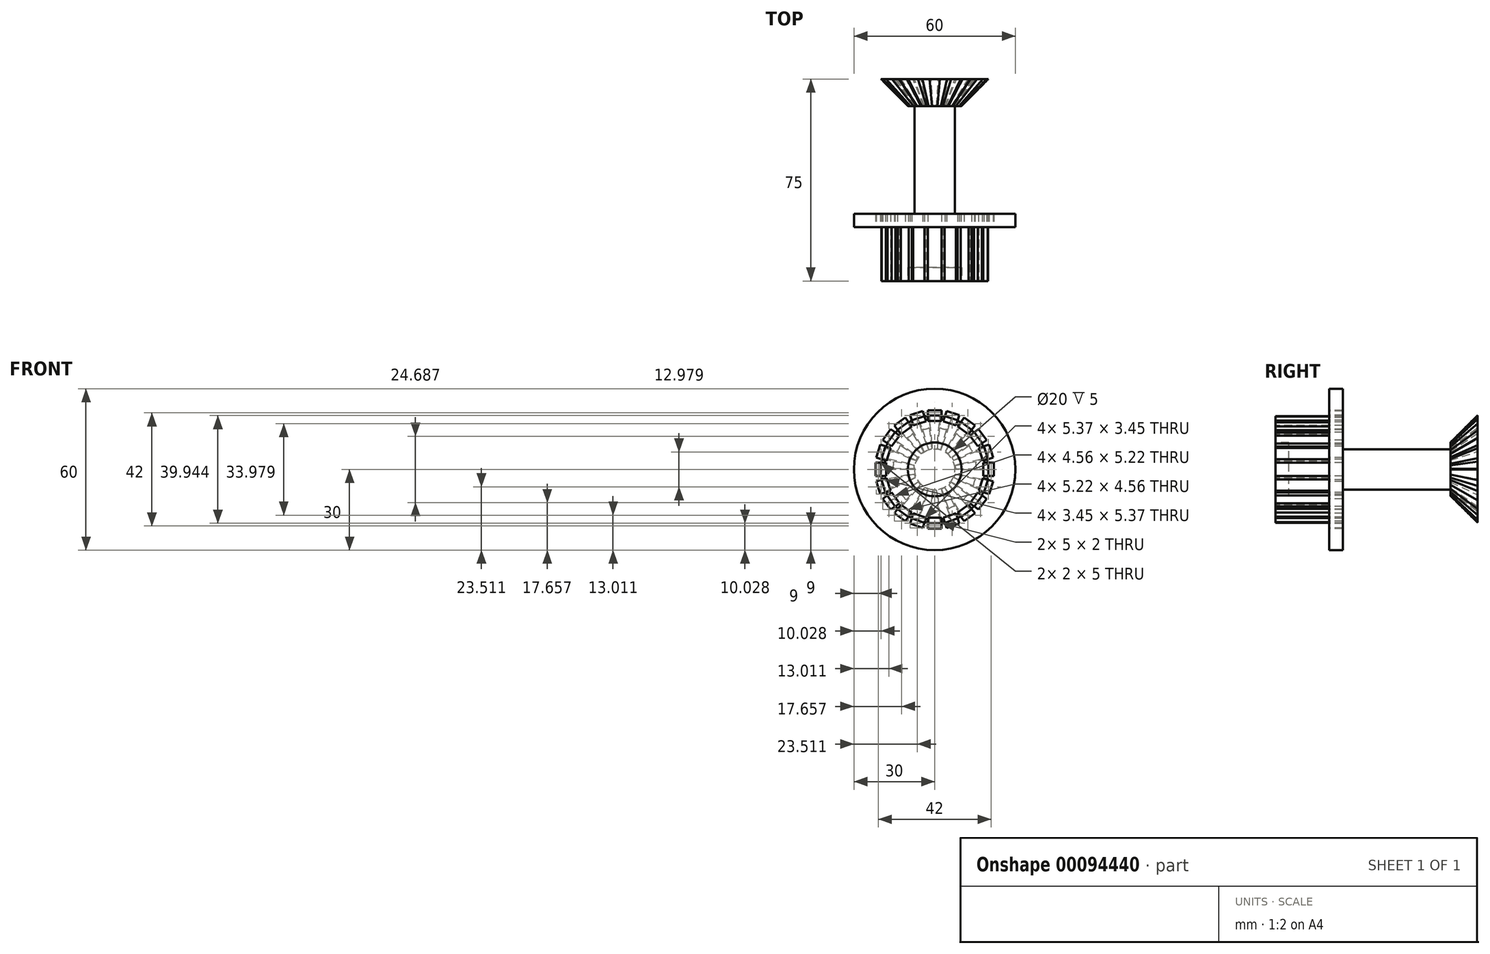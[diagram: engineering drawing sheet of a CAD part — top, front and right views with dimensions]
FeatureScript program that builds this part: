
annotation { "Feature Type Name" : "Feature", "Feature Type Description" : "" }
export const myFeature = defineFeature(function(context is Context, id is Id, definition is map)
    precondition{}
    {
        {
            var Q0;
            Q0=qCreatedBy(makeId("Front.planeOp"),FACE);
            var sketch = newSketch(context, id + "F0", { "sketchPlane" : qUnion([Q0])});
            skCircle(sketch, "E0", {"center": v(0, 0) * mm, "radius": 20 * mm});
            skSolve(sketch);
        }
        {
            var Q0;
            Q0=makeQuery(id+"F0.imprint","IMPRINT",FACE,{"disambiguationData":[TD([[makeQuery(id+"F0.imprint","IMPRINT",EDGE,{"derivedFrom":sQuery(id+"F0.wireOp",EDGE,"E0")}),1.0]])]});
            extrude(context, id + "F1", {"entities" : qUnion([Q0]), "depth" : 20 * mm});
        }
        {
            var Q0;
            Q0=makeQuery(id+"F1.opExtrude","CAP_FACE",FACE,{"disambiguationData":[OSD([sQuery(id+"F0.wireOp",EDGE,"E0")])],"isStart":true});
            var sketch = newSketch(context, id + "F2", { "sketchPlane" : qUnion([Q0])});
            skCircle(sketch, "E1", {"center": v(0, 0) * mm, "radius": 30 * mm});
            skSolve(sketch);
        }
        {
            var Q0;
            Q0 = qSketchRegion(id + "F2", true);
            extrude(context, id + "F3", {"entities" : qUnion([Q0]), "operationType" : NewBodyOperationType.ADD, "depth" : 5 * mm});
        }
        {
            var Q0;
            Q0=makeQuery(id+"F3.opExtrude","CAP_FACE",FACE,{"disambiguationData":[OSD([sQuery(id+"F2.wireOp",EDGE,"E1")])],"isStart":true});
            var sketch = newSketch(context, id + "F4", { "sketchPlane" : qUnion([Q0])});
            skLineSegment(sketch, "E2", {"start": v(-2.5, 21) * mm, "end": v(-2.5, 22) * mm});
            skLineSegment(sketch, "E3", {"start": v(-2.5, 22) * mm, "end": v(2.5, 22) * mm});
            skLineSegment(sketch, "E4", {"start": v(2.5, 22) * mm, "end": v(2.5, 20) * mm});
            skLineSegment(sketch, "E5", {"start": v(2.5, 20) * mm, "end": v(-2.5, 20) * mm});
            skLineSegment(sketch, "E6", {"start": v(-2.5, 20) * mm, "end": v(-2.5, 21) * mm});
            skLineSegment(sketch, "E7.1.0", {"start": v(-9.18, 20.15) * mm, "end": v(-4.42, 21.7) * mm});
            skLineSegment(sketch, "E7.1.1", {"start": v(-3.8, 19.8) * mm, "end": v(-8.56, 18.25) * mm});
            skLineSegment(sketch, "E7.1.2", {"start": v(-8.56, 18.25) * mm, "end": v(-8.87, 19.2) * mm});
            skLineSegment(sketch, "E7.1.3", {"start": v(-8.87, 19.2) * mm, "end": v(-9.18, 20.15) * mm});
            skLineSegment(sketch, "E7.1.4", {"start": v(-4.42, 21.7) * mm, "end": v(-3.8, 19.8) * mm});
            skLineSegment(sketch, "E7.2.0", {"start": v(-14.95, 16.33) * mm, "end": v(-10.9, 19.27) * mm});
            skLineSegment(sketch, "E7.2.1", {"start": v(-9.73, 17.65) * mm, "end": v(-13.78, 14.71) * mm});
            skLineSegment(sketch, "E7.2.2", {"start": v(-13.78, 14.71) * mm, "end": v(-14.37, 15.52) * mm});
            skLineSegment(sketch, "E7.2.3", {"start": v(-14.37, 15.52) * mm, "end": v(-14.95, 16.33) * mm});
            skLineSegment(sketch, "E7.2.4", {"start": v(-10.9, 19.27) * mm, "end": v(-9.73, 17.65) * mm});
            skLineSegment(sketch, "E7.3.0", {"start": v(-19.27, 10.9) * mm, "end": v(-16.33, 14.95) * mm});
            skLineSegment(sketch, "E7.3.1", {"start": v(-14.71, 13.78) * mm, "end": v(-17.65, 9.73) * mm});
            skLineSegment(sketch, "E7.3.2", {"start": v(-17.65, 9.73) * mm, "end": v(-18.46, 10.32) * mm});
            skLineSegment(sketch, "E7.3.3", {"start": v(-18.46, 10.32) * mm, "end": v(-19.27, 10.9) * mm});
            skLineSegment(sketch, "E7.3.4", {"start": v(-16.33, 14.95) * mm, "end": v(-14.71, 13.78) * mm});
            skLineSegment(sketch, "E7.4.0", {"start": v(-21.7, 4.42) * mm, "end": v(-20.15, 9.18) * mm});
            skLineSegment(sketch, "E7.4.1", {"start": v(-18.25, 8.56) * mm, "end": v(-19.8, 3.8) * mm});
            skLineSegment(sketch, "E7.4.2", {"start": v(-19.8, 3.8) * mm, "end": v(-20.74, 4.11) * mm});
            skLineSegment(sketch, "E7.4.3", {"start": v(-20.74, 4.11) * mm, "end": v(-21.7, 4.42) * mm});
            skLineSegment(sketch, "E7.4.4", {"start": v(-20.15, 9.18) * mm, "end": v(-18.25, 8.56) * mm});
            skLineSegment(sketch, "E7.5.0", {"start": v(-22, -2.5) * mm, "end": v(-22, 2.5) * mm});
            skLineSegment(sketch, "E7.5.1", {"start": v(-20, 2.5) * mm, "end": v(-20, -2.5) * mm});
            skLineSegment(sketch, "E7.5.2", {"start": v(-20, -2.5) * mm, "end": v(-21, -2.5) * mm});
            skLineSegment(sketch, "E7.5.3", {"start": v(-21, -2.5) * mm, "end": v(-22, -2.5) * mm});
            skLineSegment(sketch, "E7.5.4", {"start": v(-22, 2.5) * mm, "end": v(-20, 2.5) * mm});
            skLineSegment(sketch, "E7.6.0", {"start": v(-20.15, -9.18) * mm, "end": v(-21.7, -4.42) * mm});
            skLineSegment(sketch, "E7.6.1", {"start": v(-19.8, -3.8) * mm, "end": v(-18.25, -8.56) * mm});
            skLineSegment(sketch, "E7.6.2", {"start": v(-18.25, -8.56) * mm, "end": v(-19.2, -8.87) * mm});
            skLineSegment(sketch, "E7.6.3", {"start": v(-19.2, -8.87) * mm, "end": v(-20.15, -9.18) * mm});
            skLineSegment(sketch, "E7.6.4", {"start": v(-21.7, -4.42) * mm, "end": v(-19.8, -3.8) * mm});
            skLineSegment(sketch, "E7.7.0", {"start": v(-16.33, -14.95) * mm, "end": v(-19.27, -10.9) * mm});
            skLineSegment(sketch, "E7.7.1", {"start": v(-17.65, -9.73) * mm, "end": v(-14.71, -13.78) * mm});
            skLineSegment(sketch, "E7.7.2", {"start": v(-14.71, -13.78) * mm, "end": v(-15.52, -14.37) * mm});
            skLineSegment(sketch, "E7.7.3", {"start": v(-15.52, -14.37) * mm, "end": v(-16.33, -14.95) * mm});
            skLineSegment(sketch, "E7.7.4", {"start": v(-19.27, -10.9) * mm, "end": v(-17.65, -9.73) * mm});
            skLineSegment(sketch, "E7.8.0", {"start": v(-10.9, -19.27) * mm, "end": v(-14.95, -16.33) * mm});
            skLineSegment(sketch, "E7.8.1", {"start": v(-13.78, -14.71) * mm, "end": v(-9.73, -17.65) * mm});
            skLineSegment(sketch, "E7.8.2", {"start": v(-9.73, -17.65) * mm, "end": v(-10.32, -18.46) * mm});
            skLineSegment(sketch, "E7.8.3", {"start": v(-10.32, -18.46) * mm, "end": v(-10.9, -19.27) * mm});
            skLineSegment(sketch, "E7.8.4", {"start": v(-14.95, -16.33) * mm, "end": v(-13.78, -14.71) * mm});
            skLineSegment(sketch, "E7.9.0", {"start": v(-4.42, -21.7) * mm, "end": v(-9.18, -20.15) * mm});
            skLineSegment(sketch, "E7.9.1", {"start": v(-8.56, -18.25) * mm, "end": v(-3.8, -19.8) * mm});
            skLineSegment(sketch, "E7.9.2", {"start": v(-3.8, -19.8) * mm, "end": v(-4.11, -20.74) * mm});
            skLineSegment(sketch, "E7.9.3", {"start": v(-4.11, -20.74) * mm, "end": v(-4.42, -21.7) * mm});
            skLineSegment(sketch, "E7.9.4", {"start": v(-9.18, -20.15) * mm, "end": v(-8.56, -18.25) * mm});
            skLineSegment(sketch, "E7.10.0", {"start": v(2.5, -22) * mm, "end": v(-2.5, -22) * mm});
            skLineSegment(sketch, "E7.10.1", {"start": v(-2.5, -20) * mm, "end": v(2.5, -20) * mm});
            skLineSegment(sketch, "E7.10.2", {"start": v(2.5, -20) * mm, "end": v(2.5, -21) * mm});
            skLineSegment(sketch, "E7.10.3", {"start": v(2.5, -21) * mm, "end": v(2.5, -22) * mm});
            skLineSegment(sketch, "E7.10.4", {"start": v(-2.5, -22) * mm, "end": v(-2.5, -20) * mm});
            skLineSegment(sketch, "E7.11.0", {"start": v(9.18, -20.15) * mm, "end": v(4.42, -21.7) * mm});
            skLineSegment(sketch, "E7.11.1", {"start": v(3.8, -19.8) * mm, "end": v(8.56, -18.25) * mm});
            skLineSegment(sketch, "E7.11.2", {"start": v(8.56, -18.25) * mm, "end": v(8.87, -19.2) * mm});
            skLineSegment(sketch, "E7.11.3", {"start": v(8.87, -19.2) * mm, "end": v(9.18, -20.15) * mm});
            skLineSegment(sketch, "E7.11.4", {"start": v(4.42, -21.7) * mm, "end": v(3.8, -19.8) * mm});
            skLineSegment(sketch, "E7.12.0", {"start": v(14.95, -16.33) * mm, "end": v(10.9, -19.27) * mm});
            skLineSegment(sketch, "E7.12.1", {"start": v(9.73, -17.65) * mm, "end": v(13.78, -14.71) * mm});
            skLineSegment(sketch, "E7.12.2", {"start": v(13.78, -14.71) * mm, "end": v(14.37, -15.52) * mm});
            skLineSegment(sketch, "E7.12.3", {"start": v(14.37, -15.52) * mm, "end": v(14.95, -16.33) * mm});
            skLineSegment(sketch, "E7.12.4", {"start": v(10.9, -19.27) * mm, "end": v(9.73, -17.65) * mm});
            skLineSegment(sketch, "E7.13.0", {"start": v(19.27, -10.9) * mm, "end": v(16.33, -14.95) * mm});
            skLineSegment(sketch, "E7.13.1", {"start": v(14.71, -13.78) * mm, "end": v(17.65, -9.73) * mm});
            skLineSegment(sketch, "E7.13.2", {"start": v(17.65, -9.73) * mm, "end": v(18.46, -10.32) * mm});
            skLineSegment(sketch, "E7.13.3", {"start": v(18.46, -10.32) * mm, "end": v(19.27, -10.9) * mm});
            skLineSegment(sketch, "E7.13.4", {"start": v(16.33, -14.95) * mm, "end": v(14.71, -13.78) * mm});
            skLineSegment(sketch, "E7.14.0", {"start": v(21.7, -4.42) * mm, "end": v(20.15, -9.18) * mm});
            skLineSegment(sketch, "E7.14.1", {"start": v(18.25, -8.56) * mm, "end": v(19.8, -3.8) * mm});
            skLineSegment(sketch, "E7.14.2", {"start": v(19.8, -3.8) * mm, "end": v(20.74, -4.11) * mm});
            skLineSegment(sketch, "E7.14.3", {"start": v(20.74, -4.11) * mm, "end": v(21.7, -4.42) * mm});
            skLineSegment(sketch, "E7.14.4", {"start": v(20.15, -9.18) * mm, "end": v(18.25, -8.56) * mm});
            skLineSegment(sketch, "E7.15.0", {"start": v(22, 2.5) * mm, "end": v(22, -2.5) * mm});
            skLineSegment(sketch, "E7.15.1", {"start": v(20, -2.5) * mm, "end": v(20, 2.5) * mm});
            skLineSegment(sketch, "E7.15.2", {"start": v(20, 2.5) * mm, "end": v(21, 2.5) * mm});
            skLineSegment(sketch, "E7.15.3", {"start": v(21, 2.5) * mm, "end": v(22, 2.5) * mm});
            skLineSegment(sketch, "E7.15.4", {"start": v(22, -2.5) * mm, "end": v(20, -2.5) * mm});
            skLineSegment(sketch, "E7.16.0", {"start": v(20.15, 9.18) * mm, "end": v(21.7, 4.42) * mm});
            skLineSegment(sketch, "E7.16.1", {"start": v(19.8, 3.8) * mm, "end": v(18.25, 8.56) * mm});
            skLineSegment(sketch, "E7.16.2", {"start": v(18.25, 8.56) * mm, "end": v(19.2, 8.87) * mm});
            skLineSegment(sketch, "E7.16.3", {"start": v(19.2, 8.87) * mm, "end": v(20.15, 9.18) * mm});
            skLineSegment(sketch, "E7.16.4", {"start": v(21.7, 4.42) * mm, "end": v(19.8, 3.8) * mm});
            skLineSegment(sketch, "E7.17.0", {"start": v(16.33, 14.95) * mm, "end": v(19.27, 10.9) * mm});
            skLineSegment(sketch, "E7.17.1", {"start": v(17.65, 9.73) * mm, "end": v(14.71, 13.78) * mm});
            skLineSegment(sketch, "E7.17.2", {"start": v(14.71, 13.78) * mm, "end": v(15.52, 14.37) * mm});
            skLineSegment(sketch, "E7.17.3", {"start": v(15.52, 14.37) * mm, "end": v(16.33, 14.95) * mm});
            skLineSegment(sketch, "E7.17.4", {"start": v(19.27, 10.9) * mm, "end": v(17.65, 9.73) * mm});
            skLineSegment(sketch, "E7.18.0", {"start": v(10.9, 19.27) * mm, "end": v(14.95, 16.33) * mm});
            skLineSegment(sketch, "E7.18.1", {"start": v(13.78, 14.71) * mm, "end": v(9.73, 17.65) * mm});
            skLineSegment(sketch, "E7.18.2", {"start": v(9.73, 17.65) * mm, "end": v(10.32, 18.46) * mm});
            skLineSegment(sketch, "E7.18.3", {"start": v(10.32, 18.46) * mm, "end": v(10.9, 19.27) * mm});
            skLineSegment(sketch, "E7.18.4", {"start": v(14.95, 16.33) * mm, "end": v(13.78, 14.71) * mm});
            skLineSegment(sketch, "E7.19.0", {"start": v(4.42, 21.7) * mm, "end": v(9.18, 20.15) * mm});
            skLineSegment(sketch, "E7.19.1", {"start": v(8.56, 18.25) * mm, "end": v(3.8, 19.8) * mm});
            skLineSegment(sketch, "E7.19.2", {"start": v(3.8, 19.8) * mm, "end": v(4.11, 20.74) * mm});
            skLineSegment(sketch, "E7.19.3", {"start": v(4.11, 20.74) * mm, "end": v(4.42, 21.7) * mm});
            skLineSegment(sketch, "E7.19.4", {"start": v(9.18, 20.15) * mm, "end": v(8.56, 18.25) * mm});
            skPoint(sketch, "E7.center", {"position": v(0, 0) * mm});
            skSolve(sketch);
        }
        {
            var Q0;
            Q0 = qSketchRegion(id + "F4", true);
            extrude(context, id + "F5", {"entities" : qUnion([Q0]), "operationType" : NewBodyOperationType.REMOVE, "endBound" : BoundingType.THROUGH_ALL, "oppositeDirection" : true, "depth" : 25 * mm});
        }
        {
            var Q0;
            Q0=makeQuery(id+"F3.opExtrude","CAP_FACE",FACE,{"disambiguationData":[OSD([sQuery(id+"F2.wireOp",EDGE,"E1")])],"isStart":false});
            var sketch = newSketch(context, id + "F6", { "sketchPlane" : qUnion([Q0])});
            skCircle(sketch, "E8", {"center": v(0, 0) * mm, "radius": 7.5 * mm});
            skSolve(sketch);
        }
        {
            var Q0;
            Q0 = qSketchRegion(id + "F6", true);
            extrude(context, id + "F7", {"entities" : qUnion([Q0]), "operationType" : NewBodyOperationType.ADD, "depth" : 40 * mm});
        }
        {
            var Q0;
            Q0=makeQuery(id+"F1.opExtrude","CAP_FACE",FACE,{"disambiguationData":[OSD([sQuery(id+"F0.wireOp",EDGE,"E0")])],"isStart":false});
            var sketch = newSketch(context, id + "F8", { "sketchPlane" : qUnion([Q0])});
            skLineSegment(sketch, "E9.0", {"start": v(2.5, 20) * mm, "end": v(-2.5, 20) * mm});
            skLineSegment(sketch, "E10", {"start": v(2.5, 20) * mm, "end": v(2.5, 18) * mm});
            skLineSegment(sketch, "E11", {"start": v(2.5, 18) * mm, "end": v(-2.5, 18) * mm});
            skLineSegment(sketch, "E12", {"start": v(-2.5, 18) * mm, "end": v(-2.5, 20) * mm});
            skLineSegment(sketch, "E13.1.0", {"start": v(-7.94, 16.35) * mm, "end": v(-8.56, 18.25) * mm});
            skLineSegment(sketch, "E13.1.1", {"start": v(-3.18, 17.9) * mm, "end": v(-7.94, 16.35) * mm});
            skLineSegment(sketch, "E13.1.2", {"start": v(-3.8, 19.8) * mm, "end": v(-3.18, 17.9) * mm});
            skLineSegment(sketch, "E13.1.3", {"start": v(-3.8, 19.8) * mm, "end": v(-8.56, 18.25) * mm});
            skLineSegment(sketch, "E13.2.0", {"start": v(-12.6, 13.1) * mm, "end": v(-13.78, 14.71) * mm});
            skLineSegment(sketch, "E13.2.1", {"start": v(-8.56, 16.03) * mm, "end": v(-12.6, 13.1) * mm});
            skLineSegment(sketch, "E13.2.2", {"start": v(-9.73, 17.65) * mm, "end": v(-8.56, 16.03) * mm});
            skLineSegment(sketch, "E13.2.3", {"start": v(-9.73, 17.65) * mm, "end": v(-13.78, 14.71) * mm});
            skLineSegment(sketch, "E13.3.0", {"start": v(-16.03, 8.56) * mm, "end": v(-17.65, 9.73) * mm});
            skLineSegment(sketch, "E13.3.1", {"start": v(-13.1, 12.6) * mm, "end": v(-16.03, 8.56) * mm});
            skLineSegment(sketch, "E13.3.2", {"start": v(-14.71, 13.78) * mm, "end": v(-13.1, 12.6) * mm});
            skLineSegment(sketch, "E13.3.3", {"start": v(-14.71, 13.78) * mm, "end": v(-17.65, 9.73) * mm});
            skLineSegment(sketch, "E13.4.0", {"start": v(-17.9, 3.18) * mm, "end": v(-19.8, 3.8) * mm});
            skLineSegment(sketch, "E13.4.1", {"start": v(-16.35, 7.94) * mm, "end": v(-17.9, 3.18) * mm});
            skLineSegment(sketch, "E13.4.2", {"start": v(-18.25, 8.56) * mm, "end": v(-16.35, 7.94) * mm});
            skLineSegment(sketch, "E13.4.3", {"start": v(-18.25, 8.56) * mm, "end": v(-19.8, 3.8) * mm});
            skLineSegment(sketch, "E13.5.0", {"start": v(-18, -2.5) * mm, "end": v(-20, -2.5) * mm});
            skLineSegment(sketch, "E13.5.1", {"start": v(-18, 2.5) * mm, "end": v(-18, -2.5) * mm});
            skLineSegment(sketch, "E13.5.2", {"start": v(-20, 2.5) * mm, "end": v(-18, 2.5) * mm});
            skLineSegment(sketch, "E13.5.3", {"start": v(-20, 2.5) * mm, "end": v(-20, -2.5) * mm});
            skLineSegment(sketch, "E13.6.0", {"start": v(-16.35, -7.94) * mm, "end": v(-18.25, -8.56) * mm});
            skLineSegment(sketch, "E13.6.1", {"start": v(-17.9, -3.18) * mm, "end": v(-16.35, -7.94) * mm});
            skLineSegment(sketch, "E13.6.2", {"start": v(-19.8, -3.8) * mm, "end": v(-17.9, -3.18) * mm});
            skLineSegment(sketch, "E13.6.3", {"start": v(-19.8, -3.8) * mm, "end": v(-18.25, -8.56) * mm});
            skLineSegment(sketch, "E13.7.0", {"start": v(-13.1, -12.6) * mm, "end": v(-14.71, -13.78) * mm});
            skLineSegment(sketch, "E13.7.1", {"start": v(-16.03, -8.56) * mm, "end": v(-13.1, -12.6) * mm});
            skLineSegment(sketch, "E13.7.2", {"start": v(-17.65, -9.73) * mm, "end": v(-16.03, -8.56) * mm});
            skLineSegment(sketch, "E13.7.3", {"start": v(-17.65, -9.73) * mm, "end": v(-14.71, -13.78) * mm});
            skLineSegment(sketch, "E13.8.0", {"start": v(-8.56, -16.03) * mm, "end": v(-9.73, -17.65) * mm});
            skLineSegment(sketch, "E13.8.1", {"start": v(-12.6, -13.1) * mm, "end": v(-8.56, -16.03) * mm});
            skLineSegment(sketch, "E13.8.2", {"start": v(-13.78, -14.71) * mm, "end": v(-12.6, -13.1) * mm});
            skLineSegment(sketch, "E13.8.3", {"start": v(-13.78, -14.71) * mm, "end": v(-9.73, -17.65) * mm});
            skLineSegment(sketch, "E13.9.0", {"start": v(-3.18, -17.9) * mm, "end": v(-3.8, -19.8) * mm});
            skLineSegment(sketch, "E13.9.1", {"start": v(-7.94, -16.35) * mm, "end": v(-3.18, -17.9) * mm});
            skLineSegment(sketch, "E13.9.2", {"start": v(-8.56, -18.25) * mm, "end": v(-7.94, -16.35) * mm});
            skLineSegment(sketch, "E13.9.3", {"start": v(-8.56, -18.25) * mm, "end": v(-3.8, -19.8) * mm});
            skLineSegment(sketch, "E13.10.0", {"start": v(2.5, -18) * mm, "end": v(2.5, -20) * mm});
            skLineSegment(sketch, "E13.10.1", {"start": v(-2.5, -18) * mm, "end": v(2.5, -18) * mm});
            skLineSegment(sketch, "E13.10.2", {"start": v(-2.5, -20) * mm, "end": v(-2.5, -18) * mm});
            skLineSegment(sketch, "E13.10.3", {"start": v(-2.5, -20) * mm, "end": v(2.5, -20) * mm});
            skLineSegment(sketch, "E13.11.0", {"start": v(7.94, -16.35) * mm, "end": v(8.56, -18.25) * mm});
            skLineSegment(sketch, "E13.11.1", {"start": v(3.18, -17.9) * mm, "end": v(7.94, -16.35) * mm});
            skLineSegment(sketch, "E13.11.2", {"start": v(3.8, -19.8) * mm, "end": v(3.18, -17.9) * mm});
            skLineSegment(sketch, "E13.11.3", {"start": v(3.8, -19.8) * mm, "end": v(8.56, -18.25) * mm});
            skLineSegment(sketch, "E13.12.0", {"start": v(12.6, -13.1) * mm, "end": v(13.78, -14.71) * mm});
            skLineSegment(sketch, "E13.12.1", {"start": v(8.56, -16.03) * mm, "end": v(12.6, -13.1) * mm});
            skLineSegment(sketch, "E13.12.2", {"start": v(9.73, -17.65) * mm, "end": v(8.56, -16.03) * mm});
            skLineSegment(sketch, "E13.12.3", {"start": v(9.73, -17.65) * mm, "end": v(13.78, -14.71) * mm});
            skLineSegment(sketch, "E13.13.0", {"start": v(16.03, -8.56) * mm, "end": v(17.65, -9.73) * mm});
            skLineSegment(sketch, "E13.13.1", {"start": v(13.1, -12.6) * mm, "end": v(16.03, -8.56) * mm});
            skLineSegment(sketch, "E13.13.2", {"start": v(14.71, -13.78) * mm, "end": v(13.1, -12.6) * mm});
            skLineSegment(sketch, "E13.13.3", {"start": v(14.71, -13.78) * mm, "end": v(17.65, -9.73) * mm});
            skLineSegment(sketch, "E13.14.0", {"start": v(17.9, -3.18) * mm, "end": v(19.8, -3.8) * mm});
            skLineSegment(sketch, "E13.14.1", {"start": v(16.35, -7.94) * mm, "end": v(17.9, -3.18) * mm});
            skLineSegment(sketch, "E13.14.2", {"start": v(18.25, -8.56) * mm, "end": v(16.35, -7.94) * mm});
            skLineSegment(sketch, "E13.14.3", {"start": v(18.25, -8.56) * mm, "end": v(19.8, -3.8) * mm});
            skLineSegment(sketch, "E13.15.0", {"start": v(18, 2.5) * mm, "end": v(20, 2.5) * mm});
            skLineSegment(sketch, "E13.15.1", {"start": v(18, -2.5) * mm, "end": v(18, 2.5) * mm});
            skLineSegment(sketch, "E13.15.2", {"start": v(20, -2.5) * mm, "end": v(18, -2.5) * mm});
            skLineSegment(sketch, "E13.15.3", {"start": v(20, -2.5) * mm, "end": v(20, 2.5) * mm});
            skLineSegment(sketch, "E13.16.0", {"start": v(16.35, 7.94) * mm, "end": v(18.25, 8.56) * mm});
            skLineSegment(sketch, "E13.16.1", {"start": v(17.9, 3.18) * mm, "end": v(16.35, 7.94) * mm});
            skLineSegment(sketch, "E13.16.2", {"start": v(19.8, 3.8) * mm, "end": v(17.9, 3.18) * mm});
            skLineSegment(sketch, "E13.16.3", {"start": v(19.8, 3.8) * mm, "end": v(18.25, 8.56) * mm});
            skLineSegment(sketch, "E13.17.0", {"start": v(13.1, 12.6) * mm, "end": v(14.71, 13.78) * mm});
            skLineSegment(sketch, "E13.17.1", {"start": v(16.03, 8.56) * mm, "end": v(13.1, 12.6) * mm});
            skLineSegment(sketch, "E13.17.2", {"start": v(17.65, 9.73) * mm, "end": v(16.03, 8.56) * mm});
            skLineSegment(sketch, "E13.17.3", {"start": v(17.65, 9.73) * mm, "end": v(14.71, 13.78) * mm});
            skLineSegment(sketch, "E13.18.0", {"start": v(8.56, 16.03) * mm, "end": v(9.73, 17.65) * mm});
            skLineSegment(sketch, "E13.18.1", {"start": v(12.6, 13.1) * mm, "end": v(8.56, 16.03) * mm});
            skLineSegment(sketch, "E13.18.2", {"start": v(13.78, 14.71) * mm, "end": v(12.6, 13.1) * mm});
            skLineSegment(sketch, "E13.18.3", {"start": v(13.78, 14.71) * mm, "end": v(9.73, 17.65) * mm});
            skLineSegment(sketch, "E13.19.0", {"start": v(3.18, 17.9) * mm, "end": v(3.8, 19.8) * mm});
            skLineSegment(sketch, "E13.19.1", {"start": v(7.94, 16.35) * mm, "end": v(3.18, 17.9) * mm});
            skLineSegment(sketch, "E13.19.2", {"start": v(8.56, 18.25) * mm, "end": v(7.94, 16.35) * mm});
            skLineSegment(sketch, "E13.19.3", {"start": v(8.56, 18.25) * mm, "end": v(3.8, 19.8) * mm});
            skPoint(sketch, "E13.center", {"position": v(0, 0) * mm});
            skSolve(sketch);
        }
        {
            var Q0;
            Q0 = qSketchRegion(id + "F8", true);
            extrude(context, id + "F9", {"entities" : qUnion([Q0]), "operationType" : NewBodyOperationType.REMOVE, "oppositeDirection" : true, "depth" : 20 * mm});
        }
        {
            var Q0;
            Q0=makeQuery(id+"F7.opExtrude","CAP_FACE",FACE,{"disambiguationData":[OSD([sQuery(id+"F6.wireOp",EDGE,"E8")])],"isStart":false});
            cPlane(context, id + "F10", {"entities" : qUnion([Q0]), "cplaneType" : CPlaneType.OFFSET, "offset" : 10 * mm, "width" : 150 * mm, "height" : 150 * mm});
        }
        {
            var Q0;
            Q0=qCreatedBy(id+"F10.planeOp",FACE);
            var sketch = newSketch(context, id + "F11", { "sketchPlane" : qUnion([Q0])});
            skLineSegment(sketch, "E14", {"start": v(-1.94, 19.53) * mm, "end": v(-1.94, 15.53) * mm});
            skLineSegment(sketch, "E15.MirrorCS", {"start": v(1.94, 19.53) * mm, "end": v(1.94, 15.53) * mm});
            skArc(sketch, "E16", {"start": v(1.94, 19.53) * mm, "mid": v(0, 20) * mm, "end": v(-1.94, 19.53) * mm});
            skLineSegment(sketch, "E17.1.0", {"start": v(-6.17, 18.63) * mm, "end": v(-4.54, 14.97) * mm});
            skArc(sketch, "E17.1.1", {"start": v(-6.17, 18.63) * mm, "mid": v(-8.13, 18.27) * mm, "end": v(-9.72, 17.05) * mm});
            skLineSegment(sketch, "E17.1.2", {"start": v(-9.72, 17.05) * mm, "end": v(-8.09, 13.4) * mm});
            skLineSegment(sketch, "E17.2.0", {"start": v(-13.21, 14.5) * mm, "end": v(-10.24, 11.83) * mm});
            skArc(sketch, "E17.2.1", {"start": v(-13.21, 14.5) * mm, "mid": v(-14.86, 13.38) * mm, "end": v(-15.81, 11.62) * mm});
            skLineSegment(sketch, "E17.2.2", {"start": v(-15.81, 11.62) * mm, "end": v(-12.84, 8.94) * mm});
            skLineSegment(sketch, "E17.3.0", {"start": v(-17.97, 7.88) * mm, "end": v(-14.17, 6.65) * mm});
            skArc(sketch, "E17.3.1", {"start": v(-17.97, 7.88) * mm, "mid": v(-19.02, 6.18) * mm, "end": v(-19.17, 4.19) * mm});
            skLineSegment(sketch, "E17.3.2", {"start": v(-19.17, 4.19) * mm, "end": v(-15.37, 2.95) * mm});
            skLineSegment(sketch, "E17.4.0", {"start": v(-19.62, -0.1) * mm, "end": v(-15.64, 0.3) * mm});
            skArc(sketch, "E17.4.1", {"start": v(-19.62, -0.1) * mm, "mid": v(-19.9, -2.1) * mm, "end": v(-19.22, -3.97) * mm});
            skLineSegment(sketch, "E17.4.2", {"start": v(-19.22, -3.97) * mm, "end": v(-15.24, -3.56) * mm});
            skLineSegment(sketch, "E17.5.0", {"start": v(-17.88, -8.08) * mm, "end": v(-14.42, -6.08) * mm});
            skArc(sketch, "E17.5.1", {"start": v(-17.88, -8.08) * mm, "mid": v(-17.32, -10) * mm, "end": v(-15.94, -11.45) * mm});
            skLineSegment(sketch, "E17.5.2", {"start": v(-15.94, -11.45) * mm, "end": v(-12.47, -9.45) * mm});
            skLineSegment(sketch, "E17.6.0", {"start": v(-13.05, -14.65) * mm, "end": v(-10.7, -11.42) * mm});
            skArc(sketch, "E17.6.1", {"start": v(-13.05, -14.65) * mm, "mid": v(-11.76, -16.18) * mm, "end": v(-9.9, -16.94) * mm});
            skLineSegment(sketch, "E17.6.2", {"start": v(-9.9, -16.94) * mm, "end": v(-7.55, -13.7) * mm});
            skLineSegment(sketch, "E17.7.0", {"start": v(-5.96, -18.7) * mm, "end": v(-5.13, -14.78) * mm});
            skArc(sketch, "E17.7.1", {"start": v(-5.96, -18.7) * mm, "mid": v(-4.16, -19.56) * mm, "end": v(-2.16, -19.5) * mm});
            skLineSegment(sketch, "E17.7.2", {"start": v(-2.16, -19.5) * mm, "end": v(-1.33, -15.6) * mm});
            skLineSegment(sketch, "E17.8.0", {"start": v(2.16, -19.5) * mm, "end": v(1.33, -15.6) * mm});
            skArc(sketch, "E17.8.1", {"start": v(2.16, -19.5) * mm, "mid": v(4.16, -19.56) * mm, "end": v(5.96, -18.7) * mm});
            skLineSegment(sketch, "E17.8.2", {"start": v(5.96, -18.7) * mm, "end": v(5.13, -14.78) * mm});
            skLineSegment(sketch, "E17.9.0", {"start": v(9.9, -16.94) * mm, "end": v(7.55, -13.7) * mm});
            skArc(sketch, "E17.9.1", {"start": v(9.9, -16.94) * mm, "mid": v(11.76, -16.18) * mm, "end": v(13.05, -14.65) * mm});
            skLineSegment(sketch, "E17.9.2", {"start": v(13.05, -14.65) * mm, "end": v(10.7, -11.42) * mm});
            skLineSegment(sketch, "E17.10.0", {"start": v(15.94, -11.45) * mm, "end": v(12.47, -9.45) * mm});
            skArc(sketch, "E17.10.1", {"start": v(15.94, -11.45) * mm, "mid": v(17.32, -10) * mm, "end": v(17.88, -8.08) * mm});
            skLineSegment(sketch, "E17.10.2", {"start": v(17.88, -8.08) * mm, "end": v(14.42, -6.08) * mm});
            skLineSegment(sketch, "E17.11.0", {"start": v(19.22, -3.97) * mm, "end": v(15.24, -3.56) * mm});
            skArc(sketch, "E17.11.1", {"start": v(19.22, -3.97) * mm, "mid": v(19.9, -2.1) * mm, "end": v(19.62, -0.1) * mm});
            skLineSegment(sketch, "E17.11.2", {"start": v(19.62, -0.1) * mm, "end": v(15.64, 0.3) * mm});
            skLineSegment(sketch, "E17.12.0", {"start": v(19.17, 4.19) * mm, "end": v(15.37, 2.95) * mm});
            skArc(sketch, "E17.12.1", {"start": v(19.17, 4.19) * mm, "mid": v(19.02, 6.18) * mm, "end": v(17.97, 7.88) * mm});
            skLineSegment(sketch, "E17.12.2", {"start": v(17.97, 7.88) * mm, "end": v(14.17, 6.65) * mm});
            skLineSegment(sketch, "E17.13.0", {"start": v(15.81, 11.62) * mm, "end": v(12.84, 8.94) * mm});
            skArc(sketch, "E17.13.1", {"start": v(15.81, 11.62) * mm, "mid": v(14.86, 13.38) * mm, "end": v(13.21, 14.5) * mm});
            skLineSegment(sketch, "E17.13.2", {"start": v(13.21, 14.5) * mm, "end": v(10.24, 11.83) * mm});
            skLineSegment(sketch, "E17.14.0", {"start": v(9.72, 17.05) * mm, "end": v(8.09, 13.4) * mm});
            skArc(sketch, "E17.14.1", {"start": v(9.72, 17.05) * mm, "mid": v(8.13, 18.27) * mm, "end": v(6.17, 18.63) * mm});
            skLineSegment(sketch, "E17.14.2", {"start": v(6.17, 18.63) * mm, "end": v(4.54, 14.97) * mm});
            skPoint(sketch, "E17.center", {"position": v(0, 0) * mm});
            skArc(sketch, "E18", {"start": v(-4.54, 14.97) * mm, "mid": v(-3.2, 15.03) * mm, "end": v(-1.94, 15.53) * mm});
            skArc(sketch, "E19.1.0", {"start": v(-10.24, 11.83) * mm, "mid": v(-9.03, 12.43) * mm, "end": v(-8.09, 13.4) * mm});
            skArc(sketch, "E19.2.0", {"start": v(-14.17, 6.65) * mm, "mid": v(-13.3, 7.68) * mm, "end": v(-12.84, 8.94) * mm});
            skArc(sketch, "E19.3.0", {"start": v(-15.64, 0.3) * mm, "mid": v(-15.28, 1.6) * mm, "end": v(-15.37, 2.95) * mm});
            skArc(sketch, "E19.4.0", {"start": v(-14.42, -6.08) * mm, "mid": v(-14.61, -4.75) * mm, "end": v(-15.24, -3.56) * mm});
            skArc(sketch, "E19.5.0", {"start": v(-10.7, -11.42) * mm, "mid": v(-11.42, -10.28) * mm, "end": v(-12.47, -9.45) * mm});
            skArc(sketch, "E19.6.0", {"start": v(-5.13, -14.78) * mm, "mid": v(-6.25, -14.04) * mm, "end": v(-7.55, -13.7) * mm});
            skArc(sketch, "E19.7.0", {"start": v(1.33, -15.6) * mm, "mid": v(0, -15.36) * mm, "end": v(-1.33, -15.6) * mm});
            skArc(sketch, "E19.8.0", {"start": v(7.55, -13.7) * mm, "mid": v(6.25, -14.04) * mm, "end": v(5.13, -14.78) * mm});
            skArc(sketch, "E19.9.0", {"start": v(12.47, -9.45) * mm, "mid": v(11.42, -10.28) * mm, "end": v(10.7, -11.42) * mm});
            skArc(sketch, "E19.10.0", {"start": v(15.24, -3.56) * mm, "mid": v(14.61, -4.75) * mm, "end": v(14.42, -6.08) * mm});
            skArc(sketch, "E19.11.0", {"start": v(15.37, 2.95) * mm, "mid": v(15.28, 1.6) * mm, "end": v(15.64, 0.3) * mm});
            skArc(sketch, "E19.12.0", {"start": v(12.84, 8.94) * mm, "mid": v(13.3, 7.68) * mm, "end": v(14.17, 6.65) * mm});
            skArc(sketch, "E19.13.0", {"start": v(8.09, 13.4) * mm, "mid": v(9.03, 12.43) * mm, "end": v(10.24, 11.83) * mm});
            skArc(sketch, "E19.14.0", {"start": v(1.94, 15.53) * mm, "mid": v(3.2, 15.03) * mm, "end": v(4.54, 14.97) * mm});
            skSolve(sketch);
        }
        {
            var Q0;
            Q0=makeQuery(id+"F1.opExtrude","CAP_FACE",FACE,{"disambiguationData":[OSD([sQuery(id+"F0.wireOp",EDGE,"E0")])],"isStart":false});
            var sketch = newSketch(context, id + "F12", { "sketchPlane" : qUnion([Q0])});
            skCircle(sketch, "E20", {"center": v(0, 0) * mm, "radius": 10 * mm});
            skSolve(sketch);
        }
        {
            var Q0;
            Q0 = qSketchRegion(id + "F12", true);
            extrude(context, id + "F13", {"entities" : qUnion([Q0]), "operationType" : NewBodyOperationType.REMOVE, "oppositeDirection" : true, "depth" : 5 * mm});
        }
        {
            var Q0;
            Q0=makeQuery(id+"F7.opExtrude","CAP_FACE",FACE,{"disambiguationData":[OSD([sQuery(id+"F6.wireOp",EDGE,"E8")])],"isStart":false});
            var sketch = newSketch(context, id + "F14", { "sketchPlane" : qUnion([Q0])});
            skLineSegment(sketch, "E21.0", {"start": v(3.06, 9.33) * mm, "end": v(2.24, 7.5) * mm});
            skArc(sketch, "E21.1", {"start": v(-6.63, 7.27) * mm, "mid": v(-7.46, 6.7) * mm, "end": v(-7.93, 5.82) * mm});
            skArc(sketch, "E21.2", {"start": v(0.95, 9.78) * mm, "mid": v(-0.03, 10.01) * mm, "end": v(-1, 9.78) * mm});
            skArc(sketch, "E21.3", {"start": v(1.05, -9.74) * mm, "mid": v(2.05, -9.77) * mm, "end": v(2.95, -9.33) * mm});
            skArc(sketch, "E21.4", {"start": v(-9.01, 3.95) * mm, "mid": v(-9.54, 3.1) * mm, "end": v(-9.61, 2.1) * mm});
            skLineSegment(sketch, "E21.5", {"start": v(-6.63, 7.27) * mm, "end": v(-5.14, 5.93) * mm});
            skLineSegment(sketch, "E21.6", {"start": v(-3.1, 9.33) * mm, "end": v(-2.3, 7.5) * mm});
            skArc(sketch, "E21.7", {"start": v(-7.23, -3.03) * mm, "mid": v(-7.34, -2.36) * mm, "end": v(-7.64, -1.76) * mm});
            skLineSegment(sketch, "E21.8", {"start": v(-8.97, -4.03) * mm, "end": v(-7.23, -3.03) * mm});
            skLineSegment(sketch, "E21.9", {"start": v(-8, -5.7) * mm, "end": v(-6.26, -4.7) * mm});
            skArc(sketch, "E21.10", {"start": v(7.94, -5.7) * mm, "mid": v(8.63, -4.99) * mm, "end": v(8.92, -4.03) * mm});
            skLineSegment(sketch, "E21.11", {"start": v(-6.55, -7.31) * mm, "end": v(-5.37, -5.7) * mm});
            skArc(sketch, "E21.12", {"start": v(9.56, 2.1) * mm, "mid": v(9.49, 3.1) * mm, "end": v(8.96, 3.95) * mm});
            skLineSegment(sketch, "E21.13", {"start": v(4.93, -8.46) * mm, "end": v(3.75, -6.84) * mm});
            skArc(sketch, "E21.14", {"start": v(-9.84, -0.04) * mm, "mid": v(-9.97, -1.03) * mm, "end": v(-9.63, -1.97) * mm});
            skLineSegment(sketch, "E21.15", {"start": v(-7.93, 5.82) * mm, "end": v(-6.44, 4.49) * mm});
            skArc(sketch, "E21.16", {"start": v(-3, -9.33) * mm, "mid": v(-2.1, -9.77) * mm, "end": v(-1.1, -9.74) * mm});
            skArc(sketch, "E21.17", {"start": v(4.93, -8.46) * mm, "mid": v(5.85, -8.08) * mm, "end": v(6.5, -7.31) * mm});
            skArc(sketch, "E21.18", {"start": v(-5.37, -5.7) * mm, "mid": v(-5.74, -5.13) * mm, "end": v(-6.26, -4.7) * mm});
            skArc(sketch, "E21.19", {"start": v(-6.55, -7.31) * mm, "mid": v(-5.9, -8.08) * mm, "end": v(-4.98, -8.46) * mm});
            skArc(sketch, "E21.22", {"start": v(0.64, -7.78) * mm, "mid": v(-0.03, -7.67) * mm, "end": v(-0.69, -7.78) * mm});
            skArc(sketch, "E21.23", {"start": v(7.88, 5.82) * mm, "mid": v(7.4, 6.7) * mm, "end": v(6.58, 7.27) * mm});
            skArc(sketch, "E21.24", {"start": v(-8.97, -4.03) * mm, "mid": v(-8.69, -4.99) * mm, "end": v(-8, -5.7) * mm});
            skLineSegment(sketch, "E21.25", {"start": v(-4.98, -8.46) * mm, "end": v(-3.8, -6.84) * mm});
            skLineSegment(sketch, "E21.27", {"start": v(8.96, 3.95) * mm, "end": v(7.06, 3.34) * mm});
            skArc(sketch, "E21.29", {"start": v(7.66, 1.49) * mm, "mid": v(7.62, 0.82) * mm, "end": v(7.8, 0.17) * mm});
            skArc(sketch, "E21.30", {"start": v(-5.37, -5.7) * mm, "mid": v(-5.74, -5.13) * mm, "end": v(-6.26, -4.7) * mm});
            skLineSegment(sketch, "E21.31", {"start": v(3.06, 9.33) * mm, "end": v(2.24, 7.5) * mm});
            skArc(sketch, "E21.32", {"start": v(3.75, -6.84) * mm, "mid": v(3.1, -7) * mm, "end": v(2.54, -7.38) * mm});
            skArc(sketch, "E21.33", {"start": v(0.95, 9.78) * mm, "mid": v(-0.03, 10.01) * mm, "end": v(-1, 9.78) * mm});
            skLineSegment(sketch, "E21.34", {"start": v(-1, 9.78) * mm, "end": v(-1, 7.78) * mm});
            skLineSegment(sketch, "E21.36", {"start": v(-8.97, -4.03) * mm, "end": v(-7.23, -3.03) * mm});
            skLineSegment(sketch, "E21.37", {"start": v(-8, -5.7) * mm, "end": v(-6.26, -4.7) * mm});
            skArc(sketch, "E21.38", {"start": v(7.94, -5.7) * mm, "mid": v(8.63, -4.99) * mm, "end": v(8.92, -4.03) * mm});
            skArc(sketch, "E21.39", {"start": v(-9.01, 3.95) * mm, "mid": v(-9.54, 3.1) * mm, "end": v(-9.61, 2.1) * mm});
            skLineSegment(sketch, "E21.40", {"start": v(9.79, -0.04) * mm, "end": v(7.8, 0.17) * mm});
            skArc(sketch, "E21.41", {"start": v(6.4, 4.49) * mm, "mid": v(6.63, 3.86) * mm, "end": v(7.06, 3.34) * mm});
            skLineSegment(sketch, "E21.42", {"start": v(7.88, 5.82) * mm, "end": v(6.4, 4.49) * mm});
            skLineSegment(sketch, "E21.43", {"start": v(-9.61, 2.1) * mm, "end": v(-7.7, 1.49) * mm});
            skArc(sketch, "E21.45", {"start": v(-6.63, 7.27) * mm, "mid": v(-7.46, 6.7) * mm, "end": v(-7.93, 5.82) * mm});
            skArc(sketch, "E21.46", {"start": v(-7.85, 0.17) * mm, "mid": v(-7.67, 0.82) * mm, "end": v(-7.7, 1.49) * mm});
            skLineSegment(sketch, "E21.47", {"start": v(4.93, -8.46) * mm, "end": v(3.75, -6.84) * mm});
            skArc(sketch, "E21.48", {"start": v(-9.84, -0.04) * mm, "mid": v(-9.97, -1.03) * mm, "end": v(-9.63, -1.97) * mm});
            skLineSegment(sketch, "E21.50", {"start": v(2.95, -9.33) * mm, "end": v(2.54, -7.38) * mm});
            skLineSegment(sketch, "E21.51", {"start": v(7.94, -5.7) * mm, "end": v(6.21, -4.7) * mm});
            skArc(sketch, "E21.52", {"start": v(-2.3, 7.5) * mm, "mid": v(-1.62, 7.53) * mm, "end": v(-1, 7.78) * mm});
            skLineSegment(sketch, "E21.53", {"start": v(-6.63, 7.27) * mm, "end": v(-5.14, 5.93) * mm});
            skArc(sketch, "E21.54", {"start": v(7.6, -1.76) * mm, "mid": v(7.29, -2.36) * mm, "end": v(7.18, -3.03) * mm});
            skLineSegment(sketch, "E21.55", {"start": v(-3, -9.33) * mm, "end": v(-2.59, -7.38) * mm});
            skLineSegment(sketch, "E21.56", {"start": v(6.58, 7.27) * mm, "end": v(5.1, 5.93) * mm});
            skLineSegment(sketch, "E21.57", {"start": v(0.95, 9.78) * mm, "end": v(0.95, 7.78) * mm});
            skLineSegment(sketch, "E21.58", {"start": v(8.92, -4.03) * mm, "end": v(7.18, -3.03) * mm});
            skLineSegment(sketch, "E21.59", {"start": v(-9.84, -0.04) * mm, "end": v(-7.85, 0.17) * mm});
            skArc(sketch, "E21.60", {"start": v(1.05, -9.74) * mm, "mid": v(2.05, -9.77) * mm, "end": v(2.95, -9.33) * mm});
            skArc(sketch, "E21.61", {"start": v(-5.14, 5.93) * mm, "mid": v(-4.54, 6.23) * mm, "end": v(-4.07, 6.71) * mm});
            skLineSegment(sketch, "E21.62", {"start": v(-6.55, -7.31) * mm, "end": v(-5.37, -5.7) * mm});
            skArc(sketch, "E21.63", {"start": v(-7.1, 3.34) * mm, "mid": v(-6.68, 3.86) * mm, "end": v(-6.44, 4.49) * mm});
            skLineSegment(sketch, "E21.64", {"start": v(-9.63, -1.97) * mm, "end": v(-7.64, -1.76) * mm});
            skArc(sketch, "E21.65", {"start": v(-3.1, 9.33) * mm, "mid": v(-4.1, 9.15) * mm, "end": v(-4.88, 8.54) * mm});
            skLineSegment(sketch, "E21.66", {"start": v(9.56, 2.1) * mm, "end": v(7.66, 1.49) * mm});
            skArc(sketch, "E21.67", {"start": v(9.56, 2.1) * mm, "mid": v(9.49, 3.1) * mm, "end": v(8.96, 3.95) * mm});
            skLineSegment(sketch, "E21.68", {"start": v(-3.1, 9.33) * mm, "end": v(-2.3, 7.5) * mm});
            skLineSegment(sketch, "E21.70", {"start": v(4.83, 8.54) * mm, "end": v(4.02, 6.71) * mm});
            skArc(sketch, "E21.71", {"start": v(4.93, -8.46) * mm, "mid": v(5.85, -8.08) * mm, "end": v(6.5, -7.31) * mm});
            skLineSegment(sketch, "E21.73", {"start": v(9.58, -1.97) * mm, "end": v(7.6, -1.76) * mm});
            skArc(sketch, "E21.74", {"start": v(-2.59, -7.38) * mm, "mid": v(-3.15, -7) * mm, "end": v(-3.8, -6.84) * mm});
            skArc(sketch, "E21.75", {"start": v(6.21, -4.7) * mm, "mid": v(5.69, -5.13) * mm, "end": v(5.32, -5.7) * mm});
            skLineSegment(sketch, "E21.76", {"start": v(-7.93, 5.82) * mm, "end": v(-6.44, 4.49) * mm});
            skLineSegment(sketch, "E21.78", {"start": v(6.5, -7.31) * mm, "end": v(5.32, -5.7) * mm});
            skArc(sketch, "E21.79", {"start": v(4.83, 8.54) * mm, "mid": v(4.04, 9.15) * mm, "end": v(3.06, 9.33) * mm});
            skLineSegment(sketch, "E21.80", {"start": v(-9.01, 3.95) * mm, "end": v(-7.1, 3.34) * mm});
            skArc(sketch, "E21.81", {"start": v(-6.55, -7.31) * mm, "mid": v(-5.9, -8.08) * mm, "end": v(-4.98, -8.46) * mm});
            skLineSegment(sketch, "E21.83", {"start": v(1.05, -9.74) * mm, "end": v(0.64, -7.78) * mm});
            skArc(sketch, "E21.84", {"start": v(9.58, -1.97) * mm, "mid": v(9.92, -1.03) * mm, "end": v(9.79, -0.04) * mm});
            skArc(sketch, "E21.88", {"start": v(4.02, 6.71) * mm, "mid": v(4.5, 6.23) * mm, "end": v(5.1, 5.93) * mm});
            skArc(sketch, "E21.89", {"start": v(0.95, 7.78) * mm, "mid": v(1.57, 7.53) * mm, "end": v(2.24, 7.5) * mm});
            skLineSegment(sketch, "E21.90", {"start": v(-4.88, 8.54) * mm, "end": v(-4.07, 6.71) * mm});
            skLineSegment(sketch, "E21.94", {"start": v(8.92, -4.03) * mm, "end": v(7.18, -3.03) * mm});
            skLineSegment(sketch, "E21.96", {"start": v(-9.84, -0.04) * mm, "end": v(-7.85, 0.17) * mm});
            skLineSegment(sketch, "E21.98", {"start": v(1.05, -9.74) * mm, "end": v(0.64, -7.78) * mm});
            skArc(sketch, "E21.99", {"start": v(9.58, -1.97) * mm, "mid": v(9.92, -1.03) * mm, "end": v(9.79, -0.04) * mm});
            skLineSegment(sketch, "E21.102", {"start": v(6.58, 7.27) * mm, "end": v(5.1, 5.93) * mm});
            skLineSegment(sketch, "E21.103", {"start": v(-4.98, -8.46) * mm, "end": v(-3.8, -6.84) * mm});
            skLineSegment(sketch, "E21.111", {"start": v(-9.61, 2.1) * mm, "end": v(-7.7, 1.49) * mm});
            skArc(sketch, "E21.112", {"start": v(-3, -9.33) * mm, "mid": v(-2.1, -9.77) * mm, "end": v(-1.1, -9.74) * mm});
            skLineSegment(sketch, "E21.115", {"start": v(9.56, 2.1) * mm, "end": v(7.66, 1.49) * mm});
            skLineSegment(sketch, "E21.118", {"start": v(-1, 9.78) * mm, "end": v(-1, 7.78) * mm});
            skArc(sketch, "E21.121", {"start": v(-8.97, -4.03) * mm, "mid": v(-8.69, -4.99) * mm, "end": v(-8, -5.7) * mm});
            skLineSegment(sketch, "E21.122", {"start": v(2.95, -9.33) * mm, "end": v(2.54, -7.38) * mm});
            skArc(sketch, "E21.123", {"start": v(7.88, 5.82) * mm, "mid": v(7.4, 6.7) * mm, "end": v(6.58, 7.27) * mm});
            skLineSegment(sketch, "E21.124", {"start": v(7.94, -5.7) * mm, "end": v(6.21, -4.7) * mm});
            skLineSegment(sketch, "E21.125", {"start": v(9.79, -0.04) * mm, "end": v(7.8, 0.17) * mm});
            skLineSegment(sketch, "E21.126", {"start": v(7.88, 5.82) * mm, "end": v(6.4, 4.49) * mm});
            skArc(sketch, "E21.128", {"start": v(-7.23, -3.03) * mm, "mid": v(-7.34, -2.36) * mm, "end": v(-7.64, -1.76) * mm});
            skLineSegment(sketch, "E21.130", {"start": v(0.95, 9.78) * mm, "end": v(0.95, 7.78) * mm});
            skArc(sketch, "E21.132", {"start": v(-3.1, 9.33) * mm, "mid": v(-4.1, 9.15) * mm, "end": v(-4.88, 8.54) * mm});
            skLineSegment(sketch, "E21.137", {"start": v(8.96, 3.95) * mm, "end": v(7.06, 3.34) * mm});
            skLineSegment(sketch, "E21.141", {"start": v(-1.1, -9.74) * mm, "end": v(-0.69, -7.78) * mm});
            skLineSegment(sketch, "E21.142", {"start": v(4.83, 8.54) * mm, "end": v(4.02, 6.71) * mm});
            skLineSegment(sketch, "E21.144", {"start": v(-9.63, -1.97) * mm, "end": v(-7.64, -1.76) * mm});
            skArc(sketch, "E21.146", {"start": v(4.83, 8.54) * mm, "mid": v(4.04, 9.15) * mm, "end": v(3.06, 9.33) * mm});
            skLineSegment(sketch, "E21.147", {"start": v(9.58, -1.97) * mm, "end": v(7.6, -1.76) * mm});
            skLineSegment(sketch, "E21.148", {"start": v(-4.88, 8.54) * mm, "end": v(-4.07, 6.71) * mm});
            skLineSegment(sketch, "E21.155", {"start": v(-3, -9.33) * mm, "end": v(-2.59, -7.38) * mm});
            skLineSegment(sketch, "E21.161", {"start": v(-9.01, 3.95) * mm, "end": v(-7.1, 3.34) * mm});
            skLineSegment(sketch, "E21.166", {"start": v(6.5, -7.31) * mm, "end": v(5.32, -5.7) * mm});
            skArc(sketch, "E21.167", {"start": v(-2.59, -7.38) * mm, "mid": v(-3.15, -7) * mm, "end": v(-3.8, -6.84) * mm});
            skArc(sketch, "E21.173", {"start": v(-5.14, 5.93) * mm, "mid": v(-4.54, 6.23) * mm, "end": v(-4.07, 6.71) * mm});
            skArc(sketch, "E21.174", {"start": v(4.02, 6.71) * mm, "mid": v(4.5, 6.23) * mm, "end": v(5.1, 5.93) * mm});
            skArc(sketch, "E21.175", {"start": v(-7.1, 3.34) * mm, "mid": v(-6.68, 3.86) * mm, "end": v(-6.44, 4.49) * mm});
            skArc(sketch, "E21.176", {"start": v(-2.3, 7.5) * mm, "mid": v(-1.62, 7.53) * mm, "end": v(-1, 7.78) * mm});
            skArc(sketch, "E21.177", {"start": v(6.21, -4.7) * mm, "mid": v(5.69, -5.13) * mm, "end": v(5.32, -5.7) * mm});
            skArc(sketch, "E21.178", {"start": v(-7.85, 0.17) * mm, "mid": v(-7.67, 0.82) * mm, "end": v(-7.7, 1.49) * mm});
            skArc(sketch, "E21.179", {"start": v(7.66, 1.49) * mm, "mid": v(7.62, 0.82) * mm, "end": v(7.8, 0.17) * mm});
            skArc(sketch, "E21.180", {"start": v(6.4, 4.49) * mm, "mid": v(6.63, 3.86) * mm, "end": v(7.06, 3.34) * mm});
            skArc(sketch, "E21.181", {"start": v(0.64, -7.78) * mm, "mid": v(-0.03, -7.67) * mm, "end": v(-0.69, -7.78) * mm});
            skArc(sketch, "E21.182", {"start": v(3.75, -6.84) * mm, "mid": v(3.1, -7) * mm, "end": v(2.54, -7.38) * mm});
            skLineSegment(sketch, "E21.183", {"start": v(-1.1, -9.74) * mm, "end": v(-0.69, -7.78) * mm});
            skArc(sketch, "E21.184", {"start": v(7.6, -1.76) * mm, "mid": v(7.29, -2.36) * mm, "end": v(7.18, -3.03) * mm});
            skArc(sketch, "E21.185", {"start": v(0.95, 7.78) * mm, "mid": v(1.57, 7.53) * mm, "end": v(2.24, 7.5) * mm});
            skSolve(sketch);
        }
        {
            var Q1;
            Q1 = qSketchRegion(id + "F14", true);
            var Q2;
            Q2 = qSketchRegion(id + "F11", true);
            loft(context, id + "F15", {"operationType" : NewBodyOperationType.ADD, "sheetProfilesArray" : [{ "sheetProfileEntities" : qUnion([Q1]) }, { "sheetProfileEntities" : qUnion([Q2]) }]});
        }
    });
